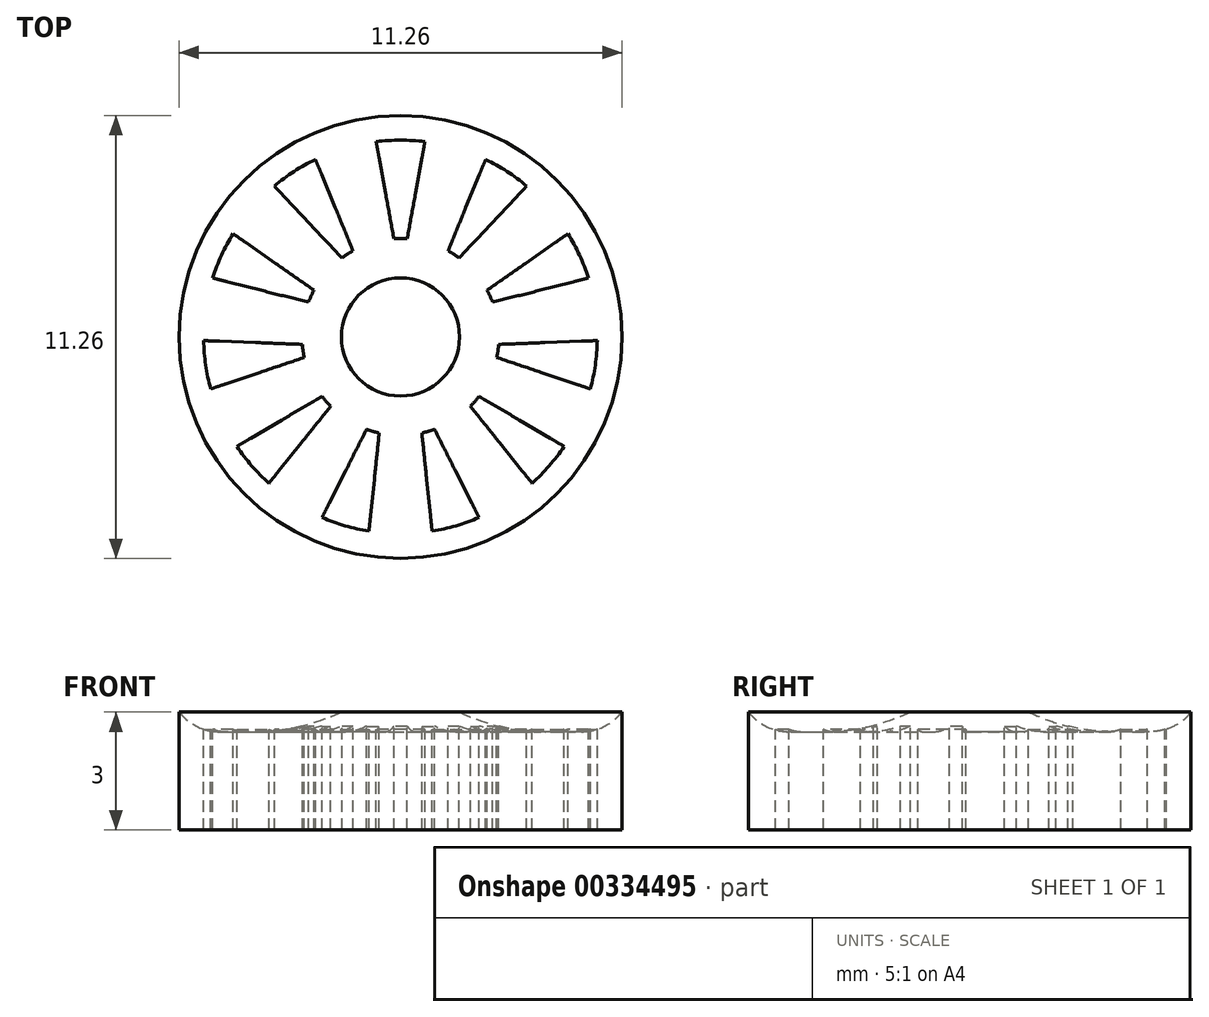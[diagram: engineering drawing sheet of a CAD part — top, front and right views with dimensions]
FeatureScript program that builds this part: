
annotation { "Feature Type Name" : "Feature", "Feature Type Description" : "" }
export const myFeature = defineFeature(function(context is Context, id is Id, definition is map)
    precondition{}
    {
        {
            var Q0;
            Q0=qCreatedBy(makeId("Front.planeOp"),FACE);
            var sketch = newSketch(context, id + "F0", { "sketchPlane" : qUnion([Q0])});
            skLineSegment(sketch, "E0.bottom", {"start": v(0, 0) * mm, "end": v(5.62, 0) * mm});
            skLineSegment(sketch, "E0.top", {"start": v(0, 0) * mm, "end": v(5.62, 0) * mm});
            skLineSegment(sketch, "E0.left", {"start": v(0, 0) * mm, "end": v(0, 0) * mm});
            skLineSegment(sketch, "E1.right", {"start": v(5.62, 0) * mm, "end": v(5.62, 3) * mm});
            skLineSegment(sketch, "E2.0", {"start": v(0, 3) * mm, "end": v(1.5, 3) * mm});
            skLineSegment(sketch, "E3", {"start": v(0, 3) * mm, "end": v(0, 0) * mm});
            skLineSegment(sketch, "E4", {"start": v(1.5, 3) * mm, "end": v(1.5, 2.5) * mm});
            skLineSegment(sketch, "E5", {"start": v(1.5, 2.5) * mm, "end": v(4.6, 2.5) * mm});
            skArc(sketch, "E6", {"start": v(4.6, 2.5) * mm, "mid": v(5.17, 2.63) * mm, "end": v(5.62, 3) * mm});
            skSolve(sketch);
        }
        {
            var Q0;
            Q0=qSketchRegion(id+"F0",true);
            var Q1;
            Q1=sQuery(id+"F0.wireOp",EDGE,"E3");
            revolve(context, id + "F1", {"entities" : qUnion([Q0]), "axis" : qUnion([Q1]), "revolveType" : RevolveType.FULL});
        }
        {
            var Q0;
            Q0=qCreatedBy(makeId("Top.planeOp"),FACE);
            cPlane(context, id + "F2", {"entities" : qUnion([Q0]), "cplaneType" : CPlaneType.OFFSET, "offset" : 3 * mm, "width" : 150 * mm, "height" : 150 * mm});
        }
        {
            var Q0;
            Q0=qCreatedBy(id+"F2.planeOp",FACE);
            var sketch = newSketch(context, id + "F3", { "sketchPlane" : qUnion([Q0])});
            skArc(sketch, "E7", {"start": v(0.17, 2.5) * mm, "mid": v(0, 2.5) * mm, "end": v(-0.17, 2.5) * mm});
            skArc(sketch, "E8", {"start": v(0.62, 4.96) * mm, "mid": v(0, 5) * mm, "end": v(-0.62, 4.96) * mm});
            skLineSegment(sketch, "E9", {"start": v(-0.62, 4.96) * mm, "end": v(-0.17, 2.5) * mm});
            skLineSegment(sketch, "E10.MirrorCS", {"start": v(0.62, 4.96) * mm, "end": v(0.17, 2.5) * mm});
            skLineSegment(sketch, "E11.1.0", {"start": v(-3.2, 3.84) * mm, "end": v(-1.49, 2) * mm});
            skLineSegment(sketch, "E11.1.1", {"start": v(-2.16, 4.5) * mm, "end": v(-1.2, 2.19) * mm});
            skArc(sketch, "E11.1.2", {"start": v(-2.16, 4.5) * mm, "mid": v(-2.7, 4.2) * mm, "end": v(-3.2, 3.84) * mm});
            skArc(sketch, "E11.1.3", {"start": v(-1.2, 2.19) * mm, "mid": v(-1.35, 2.1) * mm, "end": v(-1.49, 2) * mm});
            skLineSegment(sketch, "E11.2.0", {"start": v(-4.77, 1.5) * mm, "end": v(-2.34, 0.88) * mm});
            skLineSegment(sketch, "E11.2.1", {"start": v(-4.26, 2.62) * mm, "end": v(-2.2, 1.19) * mm});
            skArc(sketch, "E11.2.2", {"start": v(-4.26, 2.62) * mm, "mid": v(-4.55, 2.08) * mm, "end": v(-4.77, 1.5) * mm});
            skArc(sketch, "E11.2.3", {"start": v(-2.2, 1.19) * mm, "mid": v(-2.27, 1.04) * mm, "end": v(-2.34, 0.88) * mm});
            skLineSegment(sketch, "E11.3.0", {"start": v(-4.82, -1.32) * mm, "end": v(-2.45, -0.52) * mm});
            skLineSegment(sketch, "E11.3.1", {"start": v(-5, -0.1) * mm, "end": v(-2.5, -0.19) * mm});
            skArc(sketch, "E11.3.2", {"start": v(-5, -0.1) * mm, "mid": v(-4.95, -0.71) * mm, "end": v(-4.82, -1.32) * mm});
            skArc(sketch, "E11.3.3", {"start": v(-2.5, -0.19) * mm, "mid": v(-2.47, -0.36) * mm, "end": v(-2.45, -0.52) * mm});
            skLineSegment(sketch, "E11.4.0", {"start": v(-3.34, -3.72) * mm, "end": v(-1.78, -1.76) * mm});
            skLineSegment(sketch, "E11.4.1", {"start": v(-4.16, -2.78) * mm, "end": v(-2, -1.5) * mm});
            skArc(sketch, "E11.4.2", {"start": v(-4.16, -2.78) * mm, "mid": v(-3.78, -3.27) * mm, "end": v(-3.34, -3.72) * mm});
            skArc(sketch, "E11.4.3", {"start": v(-2, -1.5) * mm, "mid": v(-1.89, -1.64) * mm, "end": v(-1.78, -1.76) * mm});
            skLineSegment(sketch, "E11.5.0", {"start": v(-0.8, -4.94) * mm, "end": v(-0.54, -2.44) * mm});
            skLineSegment(sketch, "E11.5.1", {"start": v(-2, -4.59) * mm, "end": v(-0.86, -2.35) * mm});
            skArc(sketch, "E11.5.2", {"start": v(-2, -4.59) * mm, "mid": v(-1.4, -4.8) * mm, "end": v(-0.8, -4.94) * mm});
            skArc(sketch, "E11.5.3", {"start": v(-0.86, -2.35) * mm, "mid": v(-0.7, -2.4) * mm, "end": v(-0.54, -2.44) * mm});
            skLineSegment(sketch, "E11.6.0", {"start": v(2, -4.59) * mm, "end": v(0.86, -2.35) * mm});
            skLineSegment(sketch, "E11.6.1", {"start": v(0.8, -4.94) * mm, "end": v(0.54, -2.44) * mm});
            skArc(sketch, "E11.6.2", {"start": v(0.8, -4.94) * mm, "mid": v(1.4, -4.8) * mm, "end": v(2, -4.59) * mm});
            skArc(sketch, "E11.6.3", {"start": v(0.54, -2.44) * mm, "mid": v(0.7, -2.4) * mm, "end": v(0.86, -2.35) * mm});
            skLineSegment(sketch, "E11.7.0", {"start": v(4.16, -2.78) * mm, "end": v(2, -1.5) * mm});
            skLineSegment(sketch, "E11.7.1", {"start": v(3.34, -3.72) * mm, "end": v(1.78, -1.76) * mm});
            skArc(sketch, "E11.7.2", {"start": v(3.34, -3.72) * mm, "mid": v(3.78, -3.27) * mm, "end": v(4.16, -2.78) * mm});
            skArc(sketch, "E11.7.3", {"start": v(1.78, -1.76) * mm, "mid": v(1.89, -1.64) * mm, "end": v(2, -1.5) * mm});
            skLineSegment(sketch, "E11.8.0", {"start": v(5, -0.1) * mm, "end": v(2.5, -0.19) * mm});
            skLineSegment(sketch, "E11.8.1", {"start": v(4.82, -1.32) * mm, "end": v(2.45, -0.52) * mm});
            skArc(sketch, "E11.8.2", {"start": v(4.82, -1.32) * mm, "mid": v(4.95, -0.71) * mm, "end": v(5, -0.1) * mm});
            skArc(sketch, "E11.8.3", {"start": v(2.45, -0.52) * mm, "mid": v(2.47, -0.36) * mm, "end": v(2.5, -0.19) * mm});
            skLineSegment(sketch, "E11.9.0", {"start": v(4.26, 2.62) * mm, "end": v(2.2, 1.19) * mm});
            skLineSegment(sketch, "E11.9.1", {"start": v(4.77, 1.5) * mm, "end": v(2.34, 0.88) * mm});
            skArc(sketch, "E11.9.2", {"start": v(4.77, 1.5) * mm, "mid": v(4.55, 2.08) * mm, "end": v(4.26, 2.62) * mm});
            skArc(sketch, "E11.9.3", {"start": v(2.34, 0.88) * mm, "mid": v(2.27, 1.04) * mm, "end": v(2.2, 1.19) * mm});
            skLineSegment(sketch, "E11.10.0", {"start": v(2.16, 4.5) * mm, "end": v(1.2, 2.19) * mm});
            skLineSegment(sketch, "E11.10.1", {"start": v(3.2, 3.84) * mm, "end": v(1.49, 2) * mm});
            skArc(sketch, "E11.10.2", {"start": v(3.2, 3.84) * mm, "mid": v(2.7, 4.2) * mm, "end": v(2.16, 4.5) * mm});
            skArc(sketch, "E11.10.3", {"start": v(1.49, 2) * mm, "mid": v(1.35, 2.1) * mm, "end": v(1.2, 2.19) * mm});
            skSolve(sketch);
        }
        {
            var Q0;
            Q0=qSketchRegion(id+"F3",true);
            extrude(context, id + "F4", {"entities" : qUnion([Q0]), "operationType" : NewBodyOperationType.REMOVE, "oppositeDirection" : true, "depth" : 25 * mm});
        }
        {
            var Q0;
            Q0=makeQuery(id+"F1.opRevolve","SWEPT_EDGE",EDGE,{"disambiguationData":[OSD([sQuery(id+"F0.wireOp",EDGE,"E4"),sQuery(id+"F0.wireOp",EDGE,"E5")])]});
            fillet(context, id + "F5", {"entities" : qUnion([Q0]), "radius" : 5 * mm, "tangentPropagation" : true, "allowEdgeOverflow" : false});
        }
    });
